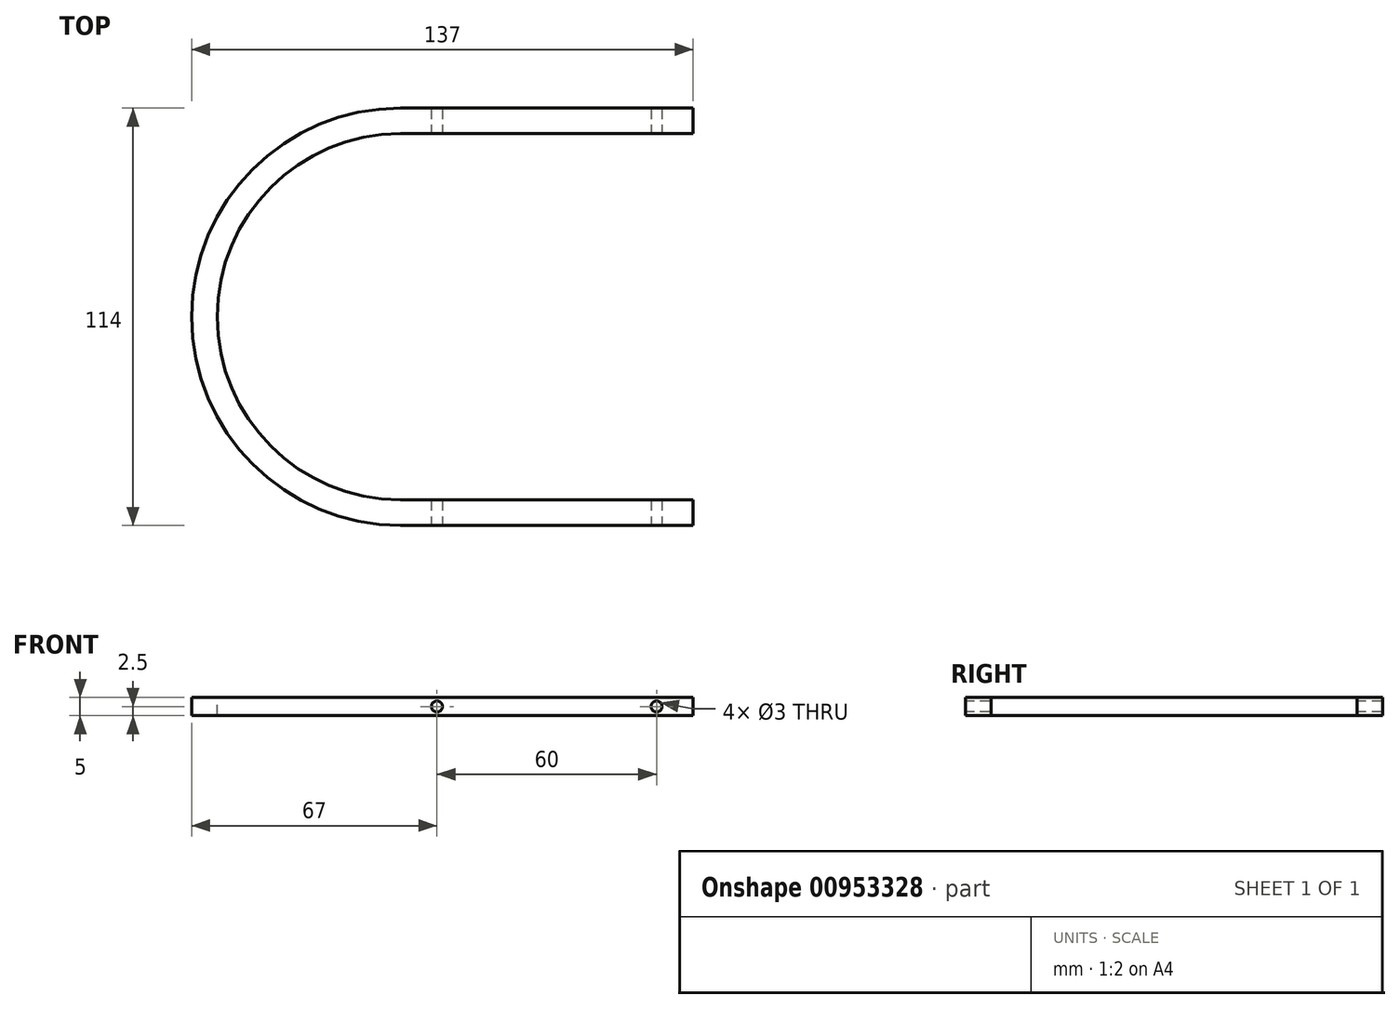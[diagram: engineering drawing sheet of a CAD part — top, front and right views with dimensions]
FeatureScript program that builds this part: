
annotation { "Feature Type Name" : "Feature", "Feature Type Description" : "" }
export const myFeature = defineFeature(function(context is Context, id is Id, definition is map)
    precondition{}
    {
        {
            var Q0;
            Q0=qCreatedBy(makeId("Top.planeOp"),FACE);
            var sketch = newSketch(context, id + "F0", { "sketchPlane" : qUnion([Q0])});
            skLineSegment(sketch, "E0.bottom", {"start": v(40, -50) * mm, "end": v(-40, -50) * mm});
            skLineSegment(sketch, "E0.top", {"start": v(40, 50) * mm, "end": v(-40, 50) * mm});
            skPoint(sketch, "E0.middle", {"position": v(0, 0) * mm});
            skArc(sketch, "E1", {"start": v(-40, 50) * mm, "mid": v(-90, 0) * mm, "end": v(-40, -50) * mm});
            skLineSegment(sketch, "E2.0", {"start": v(40, -57) * mm, "end": v(-40, -57) * mm});
            skArc(sketch, "E2.1", {"start": v(-40, 57) * mm, "mid": v(-97, 0) * mm, "end": v(-40, -57) * mm});
            skLineSegment(sketch, "E2.2", {"start": v(40, 57) * mm, "end": v(-40, 57) * mm});
            skLineSegment(sketch, "E3", {"start": v(40, 50) * mm, "end": v(40, 57) * mm});
            skLineSegment(sketch, "E4", {"start": v(40, -50) * mm, "end": v(40, -57) * mm});
            skSolve(sketch);
        }
        {
            var Q0;
            Q0 = qSketchRegion(id + "F0", true);
            extrude(context, id + "F1", {"entities" : qUnion([Q0]), "oppositeDirection" : true, "depth" : 5 * mm, "offsetDistance" : 25 * mm});
        }
        {
            var Q0;
            Q0=makeQuery(id+"F1.opExtrude","SWEPT_FACE",FACE,{"disambiguationData":[OSD([sQuery(id+"F0.wireOp",EDGE,"E2.0")])]});
            var sketch = newSketch(context, id + "F2", { "sketchPlane" : qUnion([Q0])});
            skCircle(sketch, "E5", {"center": v(30, -2.5) * mm, "radius": 1.5 * mm});
            skCircle(sketch, "E6", {"center": v(-30, -2.5) * mm, "radius": 1.5 * mm});
            skSolve(sketch);
        }
        {
            var Q0;
            Q0=makeQuery(id+"F2.imprint","IMPRINT",FACE,{"disambiguationData":[TD([[makeQuery(id+"F2.imprint","IMPRINT",EDGE,{"derivedFrom":sQuery(id+"F2.wireOp",EDGE,"E6")}),1.0]])]});
            var Q1;
            Q1=makeQuery(id+"F2.imprint","IMPRINT",FACE,{"disambiguationData":[TD([[makeQuery(id+"F2.imprint","IMPRINT",EDGE,{"derivedFrom":sQuery(id+"F2.wireOp",EDGE,"E5")}),1.0]])]});
            extrude(context, id + "F3", {"entities" : qUnion([Q0, Q1]), "operationType" : NewBodyOperationType.REMOVE, "oppositeDirection" : true, "depth" : 150 * mm, "offsetDistance" : 25 * mm});
        }
    });
